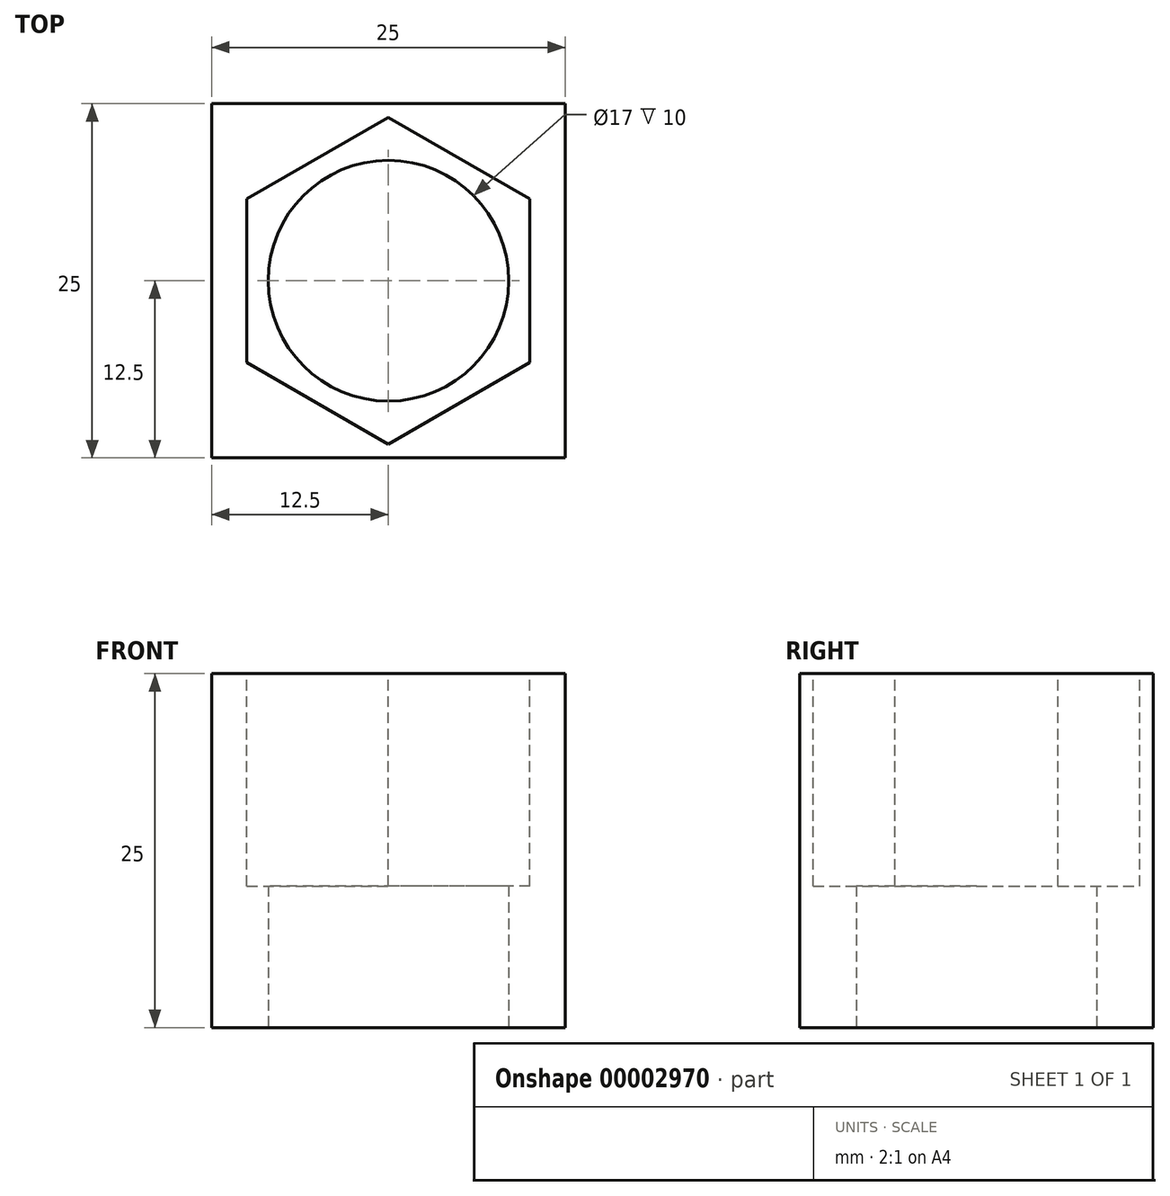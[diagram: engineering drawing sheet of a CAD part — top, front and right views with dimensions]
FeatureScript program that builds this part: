
annotation { "Feature Type Name" : "Feature", "Feature Type Description" : "" }
export const myFeature = defineFeature(function(context is Context, id is Id, definition is map)
    precondition{}
    {
        {
            var Q0;
            Q0=qCreatedBy(makeId("Top.planeOp"),FACE);
            var sketch = newSketch(context, id + "F0", { "sketchPlane" : qUnion([Q0])});
            skLineSegment(sketch, "E0.rect.bottom", {"start": v(12.5, -12.5) * mm, "end": v(-12.5, -12.5) * mm});
            skLineSegment(sketch, "E0.rect.top", {"start": v(12.5, 12.5) * mm, "end": v(-12.5, 12.5) * mm});
            skLineSegment(sketch, "E0.rect.left", {"start": v(12.5, -12.5) * mm, "end": v(12.5, 12.5) * mm});
            skLineSegment(sketch, "E0.rect.right", {"start": v(-12.5, -12.5) * mm, "end": v(-12.5, 12.5) * mm});
            skPoint(sketch, "E0.rect.middle", {"position": v(0, 0) * mm});
            skSolve(sketch);
        }
        {
            var Q0;
            Q0 = qSketchRegion(id + "F0", true);
            extrude(context, id + "F1", {"entities" : qUnion([Q0]), "depth" : 25 * mm});
        }
        {
            var Q0;
            Q0=makeQuery(id+"F1.opExtrude","CAP_FACE",FACE,{"disambiguationData":[OSD([sQuery(id+"F0.wireOp",EDGE,"E0.rect.bottom"),sQuery(id+"F0.wireOp",EDGE,"E0.rect.top"),sQuery(id+"F0.wireOp",EDGE,"E0.rect.left"),sQuery(id+"F0.wireOp",EDGE,"E0.rect.right")])],"isStart":false});
            var sketch = newSketch(context, id + "F2", { "sketchPlane" : qUnion([Q0])});
            skLineSegment(sketch, "E1", {"start": v(0, 0) * mm, "end": v(0, 12.94) * mm, "construction": true});
            skLineSegment(sketch, "E2", {"start": v(0, 0) * mm, "end": v(-8.71, 15.1) * mm, "construction": true});
            skCircle(sketch, "E3.cCircle", {"center": v(0, 0) * mm, "radius": 10 * mm, "construction": true});
            skLineSegment(sketch, "E3.0", {"start": v(-10, 5.77) * mm, "end": v(0, 11.55) * mm});
            skLineSegment(sketch, "E3.1", {"start": v(0, 11.55) * mm, "end": v(10, 5.77) * mm});
            skLineSegment(sketch, "E3.2", {"start": v(10, 5.77) * mm, "end": v(10, -5.77) * mm});
            skLineSegment(sketch, "E3.3", {"start": v(10, -5.77) * mm, "end": v(0, -11.55) * mm});
            skLineSegment(sketch, "E3.4", {"start": v(0, -11.55) * mm, "end": v(-10, -5.77) * mm});
            skLineSegment(sketch, "E3.5", {"start": v(-10, -5.77) * mm, "end": v(-10, 5.77) * mm});
            skPoint(sketch, "E3.0.midPoint", {"position": v(-5, 8.66) * mm});
            skSolve(sketch);
        }
        {
            var Q0;
            Q0=makeQuery(id+"F2.imprint","IMPRINT",FACE,{"disambiguationData":[TD([[makeQuery(id+"F2.imprint","IMPRINT",EDGE,{"derivedFrom":sQuery(id+"F2.wireOp",EDGE,"E3.0")}),-1.0]])]});
            extrude(context, id + "F3", {"entities" : qUnion([Q0]), "operationType" : NewBodyOperationType.REMOVE, "oppositeDirection" : true, "depth" : 15 * mm});
        }
        {
            var Q0;
            Q0=makeQuery(id+"F1.opExtrude","CAP_FACE",FACE,{"disambiguationData":[OSD([sQuery(id+"F0.wireOp",EDGE,"E0.rect.bottom"),sQuery(id+"F0.wireOp",EDGE,"E0.rect.top"),sQuery(id+"F0.wireOp",EDGE,"E0.rect.left"),sQuery(id+"F0.wireOp",EDGE,"E0.rect.right")])],"isStart":true});
            var sketch = newSketch(context, id + "F4", { "sketchPlane" : qUnion([Q0])});
            skCircle(sketch, "E4", {"center": v(0, 0) * mm, "radius": 8.5 * mm});
            skSolve(sketch);
        }
        {
            var Q0;
            Q0 = qSketchRegion(id + "F4", true);
            extrude(context, id + "F5", {"entities" : qUnion([Q0]), "operationType" : NewBodyOperationType.REMOVE, "endBound" : BoundingType.THROUGH_ALL, "oppositeDirection" : true, "depth" : 7.92 * mm});
        }
    });
